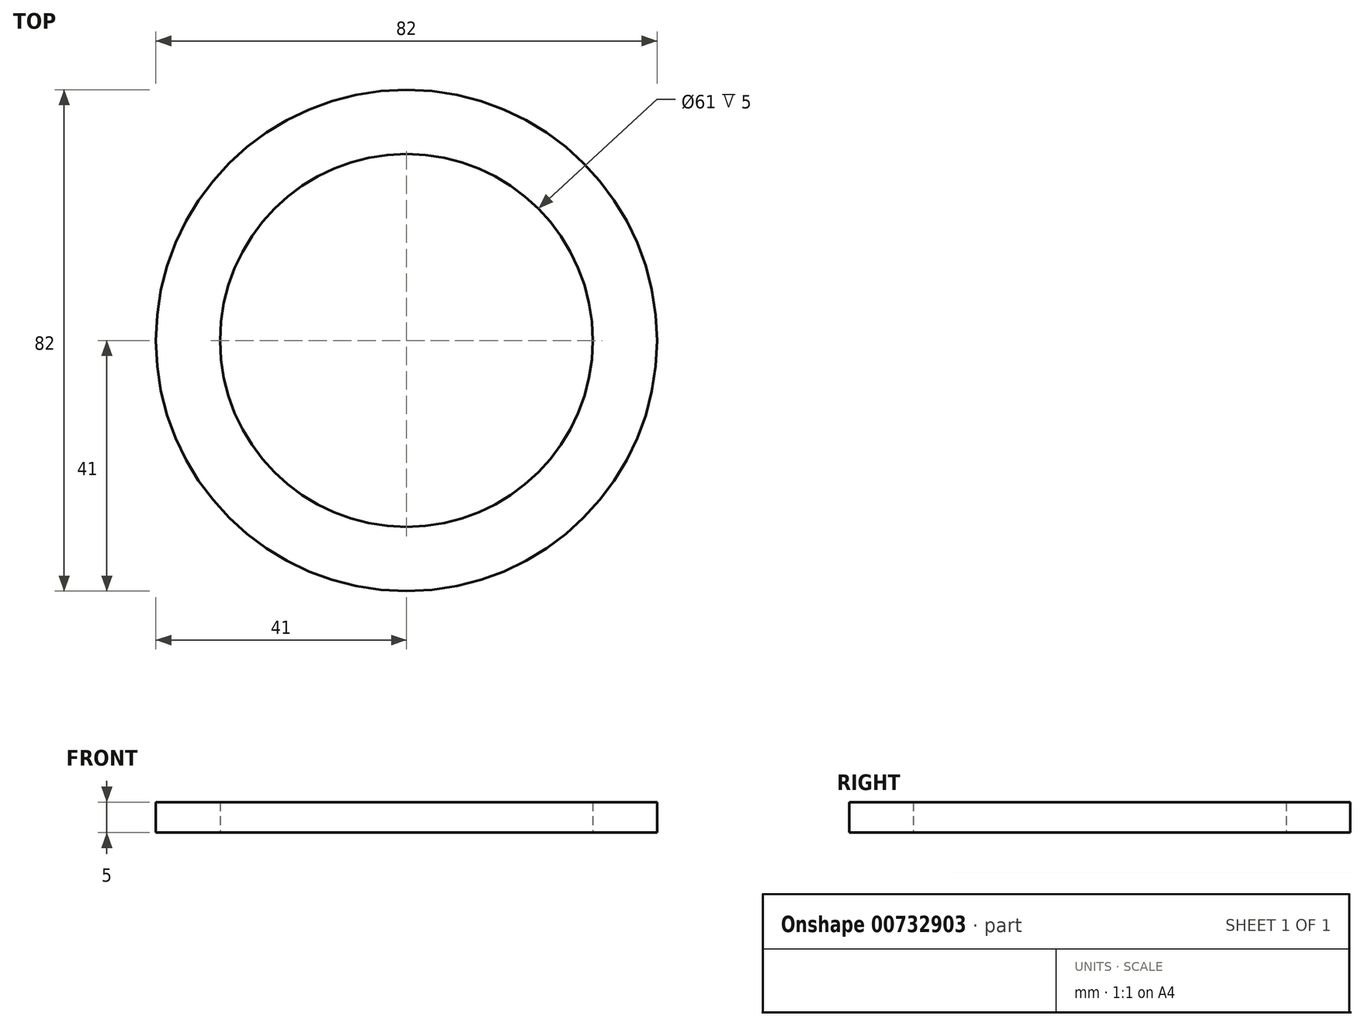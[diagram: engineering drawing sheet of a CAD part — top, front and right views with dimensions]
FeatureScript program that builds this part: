
annotation { "Feature Type Name" : "Feature", "Feature Type Description" : "" }
export const myFeature = defineFeature(function(context is Context, id is Id, definition is map)
    precondition{}
    {
        {
            var Q0;
            Q0=qCreatedBy(makeId("Top.planeOp"),FACE);
            var sketch = newSketch(context, id + "F0", { "sketchPlane" : qUnion([Q0])});
            skCircle(sketch, "E0", {"center": v(0, 0) * mm, "radius": 30.5 * mm});
            skCircle(sketch, "E1", {"center": v(0, 0) * mm, "radius": 41 * mm});
            skSolve(sketch);
        }
        {
            var Q0;
            Q0=makeQuery(id+"F0.imprint","IMPRINT",FACE,{"disambiguationData":[TD([[makeQuery(id+"F0.imprint","IMPRINT",EDGE,{"derivedFrom":sQuery(id+"F0.wireOp",EDGE,"E0")}),-1.0]])]});
            extrude(context, id + "F1", {"entities" : qUnion([Q0]), "depth" : 5 * mm, "offsetDistance" : 25 * mm});
        }
    });
